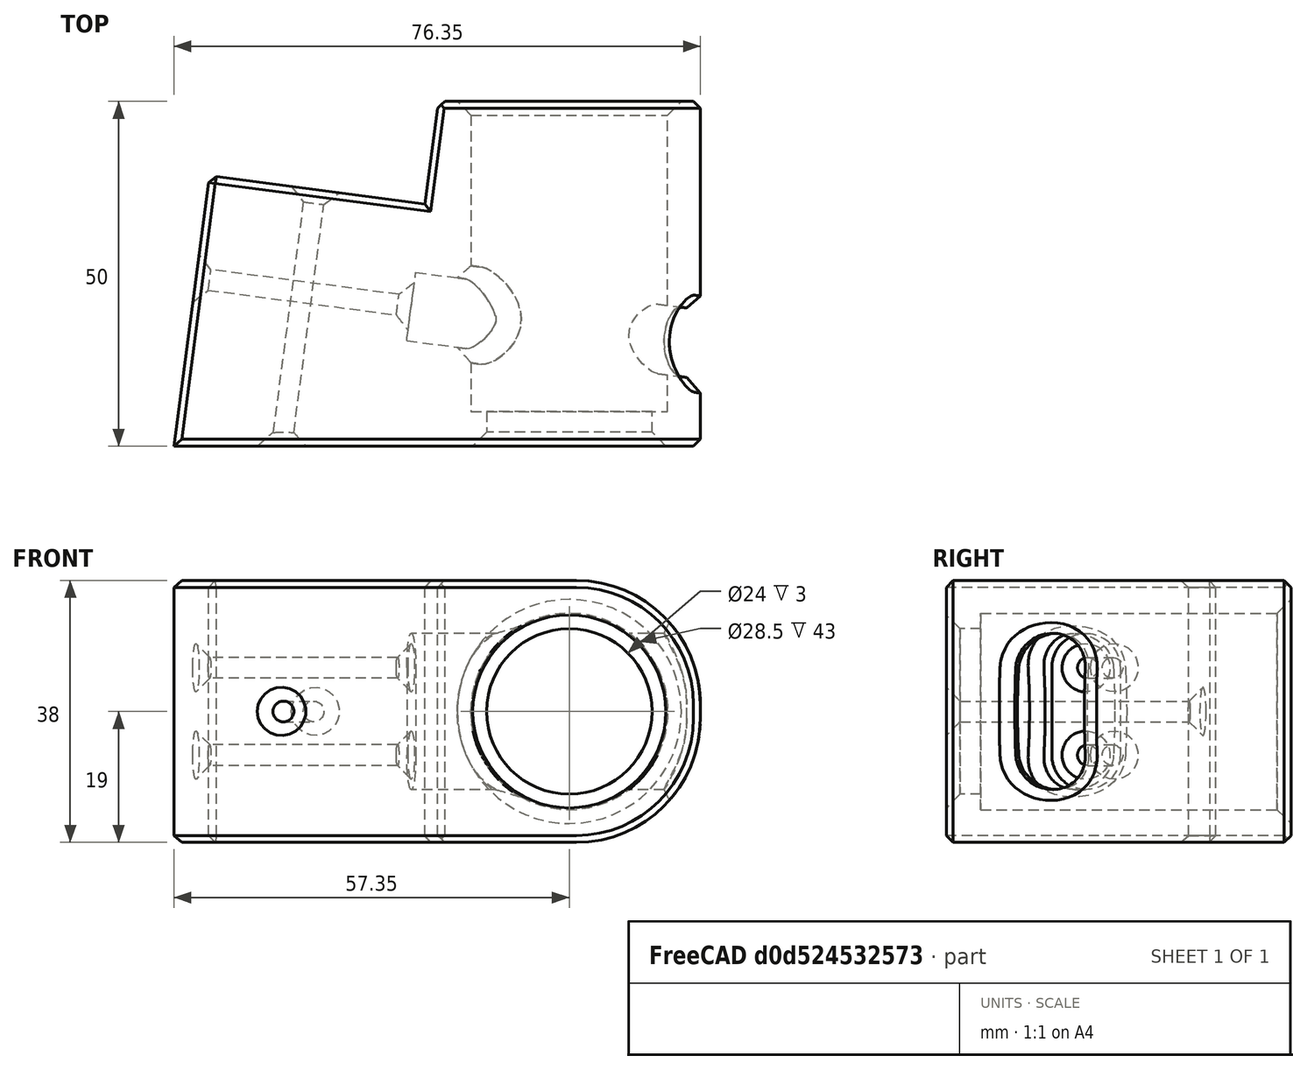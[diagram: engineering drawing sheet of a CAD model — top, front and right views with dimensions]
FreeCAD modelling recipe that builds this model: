
FCSTD DOCUMENT  (FreeCAD 0.18R16110 (Git))
Label: Support_solar_V3
License: All rights reserved
LicenseURL: http://en.wikipedia.org/wiki/All_rights_reserved
objects: PartDesign::Chamfer×13, Sketcher::SketchObject×10, PartDesign::Pocket×6, PartDesign::Pad×4, PartDesign::Fillet×1, PartDesign::Plane×1, PartDesign::Body×1, Mesh::Feature×1
note: 46 computed .brp shape members not serialized (recipe doc carries the construction recipe); baked Part::Feature solids carry a one-line shape summary decoded from their .brp

FEATURE [Sketcher::SketchObject] Sketch
  MapMode = 5
  Support = -> [XY_Plane]
  sketch-geometry (7):
    g0: LineSegment StartX=19 StartY=0 StartZ=0 EndX=-19 EndY=0 EndZ=0
    g1: LineSegment StartX=-61.9779 StartY=-85.1185 StartZ=0 EndX=-19 EndY=-90.7766 EndZ=0
    g2: LineSegment StartX=-19 StartY=-90.7766 StartZ=0 EndX=19 EndY=-90.7766 EndZ=0
    g3: LineSegment StartX=19 StartY=-90.7766 StartZ=0 EndX=19 EndY=0 EndZ=0
    g4: LineSegment StartX=-19 StartY=0 StartZ=0 EndX=-20.9579 EndY=-14.8717 EndZ=0
    g5: LineSegment StartX=-20.9579 StartY=-14.8717 StartZ=0 EndX=-52.1884 EndY=-10.7601 EndZ=0
    g6: LineSegment StartX=-52.1884 StartY=-10.7601 StartZ=0 EndX=-61.9779 EndY=-85.1185 EndZ=0
  constraints (20):
    c: PointOnObject(g0,g-1)
    c: Coincident(g1,g2)
    c: Horizontal(g2)
    c: Coincident(g2,g3)
    c: Coincident(g3,g0)
    c: Vertical(g3)
    c: Coincident(g0,g4)
    c: Coincident(g4,g5)
    c: Coincident(g5,g6)
    c: Coincident(g6,g1)
    c: Angle(g4,g0) = 1.7017
    c: Perpendicular(g4,g5)
    c: Perpendicular(g5,g6)
    c: Perpendicular(g1,g6)
    c: Distance(g5) = 31.5
    c: Distance(g4) = 15
    c: DistanceX(g0,g0) = 38
    c: Distance(g6) = 75
    c: Equal(g2,g0)
    c: Symmetric(g0,g0,g-2)
FEATURE [PartDesign::Pad] Pad
  Length = 38
  Length2 = 100
  Profile = -> Sketch
  Type = 0
FEATURE [Sketcher::SketchObject] Sketch001
  MapMode = 5
  Placement = pos=(0,0,0) rot=(0,0.707107,0.707107;3.14159rad)
  Support = -> [Pad]
  sketch-geometry (1):
    g0: Circle CenterX=0 CenterY=19 CenterZ=0 NormalX=0 NormalY=0 NormalZ=1 AngleXU=0 Radius=14.25
  constraints (3):
    c: Radius(g0) = 14.25
    c: Distance(g-1,g0) = 19
    c: PointOnObject(g0,g-2)
FEATURE [PartDesign::Pocket] Pocket
  BaseFeature = -> Pad
  Length = 100
  Length2 = 100
  Profile = -> Sketch001
  Type = 0
FEATURE [PartDesign::Fillet] Fillet
  Base = -> Pocket [Edge7,Edge8]
  BaseFeature = -> Pocket
  Radius = 18
FEATURE [Sketcher::SketchObject] Sketch002
  ExternalGeometry = -> [Fillet]
  MapMode = 5
  Placement = pos=(-49.9068,6.57036,0) rot=(-0.527011,0.600941,0.600941;4.11164rad)
  Support = -> [Fillet]
  sketch-geometry (4):
    g0: Circle CenterX=32.48 CenterY=25.3333 CenterZ=0 NormalX=0 NormalY=0 NormalZ=1 AngleXU=0 Radius=1.5
    g1: Circle CenterX=32.48 CenterY=12.6667 CenterZ=0 NormalX=0 NormalY=0 NormalZ=1 AngleXU=0 Radius=1.5
    g2: Circle CenterX=77.48 CenterY=25.3333 CenterZ=0 NormalX=0 NormalY=0 NormalZ=1 AngleXU=0 Radius=1.5
    g3: Circle CenterX=77.48 CenterY=12.6667 CenterZ=0 NormalX=0 NormalY=0 NormalZ=1 AngleXU=0 Radius=1.5
  constraints (12):
    c: Radius(g3) = 1.5
    c: Equal(g3,g2)
    c: Equal(g3,g0)
    c: Equal(g3,g1)
    c: Distance(g0,g-3) = 15
    c: Distance(g1,g-3) = 15
    c: Distance(g2,g-5) = 15
    c: Distance(g3,g-5) = 15
    c: DistanceY(g-1,g1) = 12.6667
    c: Distance(g0,g-4) = 12.6667
    c: Distance(g2,g-4) = 12.6667
    c: DistanceY(g-1,g3) = 12.6667
FEATURE [PartDesign::Pocket] Pocket001
  BaseFeature = -> Fillet
  Length = 100
  Length2 = 100
  Profile = -> Sketch002
  Type = 0
FEATURE [PartDesign::Plane] DatumPlane
  Length = 81.0007
  MapMode = 5
  Placement = pos=(-18.6763,2.45878,0) rot=(-0.527011,0.600941,0.600941;4.11164rad)
  ResizeMode = 0
  Support = -> [Pocket001]
  Width = 59.5477
FEATURE [Sketcher::SketchObject] Sketch003
  ExternalGeometry = -> [Pocket001]
  MapMode = 5
  Placement = pos=(-18.6763,2.45878,0) rot=(-0.527011,0.600941,0.600941;4.11164rad)
  Support = -> [DatumPlane]
  sketch-geometry (8):
    g0: ArcOfCircle CenterX=32.48 CenterY=25.3333 CenterZ=0 NormalX=0 NormalY=0 NormalZ=1 AngleXU=0 Radius=5 StartAngle=1.1e-15 EndAngle=3.14159
    g1: ArcOfCircle CenterX=32.48 CenterY=12.6667 CenterZ=0 NormalX=0 NormalY=0 NormalZ=1 AngleXU=0 Radius=5 StartAngle=3.14159 EndAngle=6.28319
    g2: LineSegment StartX=27.48 StartY=25.3333 StartZ=0 EndX=27.48 EndY=12.6667 EndZ=0
    g3: LineSegment StartX=37.48 StartY=25.3333 StartZ=0 EndX=37.48 EndY=12.6667 EndZ=0
    g4: ArcOfCircle CenterX=77.48 CenterY=25.3333 CenterZ=0 NormalX=0 NormalY=0 NormalZ=1 AngleXU=0 Radius=5 StartAngle=0 EndAngle=3.14159
    g5: ArcOfCircle CenterX=77.48 CenterY=12.6667 CenterZ=0 NormalX=0 NormalY=0 NormalZ=1 AngleXU=0 Radius=5 StartAngle=3.14159 EndAngle=6.28319
    g6: LineSegment StartX=72.48 StartY=25.3333 StartZ=0 EndX=72.48 EndY=12.6667 EndZ=0
    g7: LineSegment StartX=82.48 StartY=25.3333 StartZ=0 EndX=82.48 EndY=12.6667 EndZ=0
  constraints (16):
    c: Tangent(g0,g3) = 1.5708
    c: Tangent(g0,g2) = -1.5708
    c: Tangent(g2,g1) = -1.5708
    c: Tangent(g3,g1) = 1.5708
    c: Vertical(g2)
    c: Coincident(g0,g-3)
    c: Coincident(g1,g-4)
    c: Radius(g1) = 5
    c: Tangent(g4,g7) = 1.5708
    c: Tangent(g4,g6) = -1.5708
    c: Tangent(g6,g5) = -1.5708
    c: Tangent(g7,g5) = 1.5708
    c: Vertical(g6)
    c: Coincident(g4,g-5)
    c: Coincident(g5,g-6)
    c: Radius(g5) = 5
FEATURE [PartDesign::Pocket] Pocket002
  BaseFeature = -> Pocket001
  Length = 70
  Length2 = 100
  Profile = -> Sketch003
  Type = 0
FEATURE [Sketcher::SketchObject] Sketch004
  ExternalGeometry = -> [Pocket002,DatumPlane]
  MapMode = 5
  Placement = pos=(-2.2816,-17.3305,0) rot=(0.046297,0.706349,0.706349;3.04907rad)
  Support = -> [Pocket002]
  sketch-geometry (1):
    g0: Circle CenterX=34.8375 CenterY=19 CenterZ=0 NormalX=0 NormalY=0 NormalZ=1 AngleXU=0 Radius=1.5
  constraints (3):
    c: Radius(g0) = 1.5
    c: Distance(g0,g-3) = 19
    c: Distance(g0,g-4) = 15.5
FEATURE [PartDesign::Pocket] Pocket003
  BaseFeature = -> Pocket002
  Length = 50
  Length2 = 100
  Profile = -> Sketch004
  Type = 0
FEATURE [PartDesign::Chamfer] Chamfer
  Base = -> Pocket003 [Edge80,Edge82,Edge83,Edge85,Edge84]
  BaseFeature = -> Pocket003
  Size = 2
FEATURE [PartDesign::Chamfer] Chamfer001
  Base = -> Chamfer [Edge52,Edge48]
  BaseFeature = -> Chamfer
  Size = 2
FEATURE [PartDesign::Chamfer] Chamfer002
  Base = -> Chamfer001 [Edge70]
  BaseFeature = -> Chamfer001
  Size = 2
FEATURE [PartDesign::Chamfer] Chamfer003
  Base = -> Chamfer002 [Edge11]
  BaseFeature = -> Chamfer002
  Size = 2
FEATURE [PartDesign::Chamfer] Chamfer004
  Base = -> Chamfer003 [Edge11]
  BaseFeature = -> Chamfer003
  Size = 2
FEATURE [PartDesign::Chamfer] Chamfer005
  Base = -> Chamfer004 [Edge84]
  BaseFeature = -> Chamfer004
  Size = 1
FEATURE [Sketcher::SketchObject] Sketch006
  MapMode = 5
  Placement = pos=(0,0,38) rot=(0,0,1;0rad)
  sketch-geometry (3):
    g0: LineSegment StartX=1 StartY=-90.7766 StartZ=0 EndX=-61.6371 EndY=-82.5303 EndZ=0
    g1: LineSegment StartX=-61.6371 StartY=-82.5303 StartZ=0 EndX=-62.7228 EndY=-90.7766 EndZ=0
    g2: LineSegment StartX=-62.7228 StartY=-90.7766 StartZ=0 EndX=1 EndY=-90.7766 EndZ=0
  constraints (5):
    c: Coincident(g0,g1)
    c: Coincident(g1,g2)
    c: Coincident(g2,g0)
    c: Horizontal(g2)
    c: Perpendicular(g1,g0)
FEATURE [PartDesign::Pad] Pad002
  BaseFeature = -> Chamfer005
  Length = 38
  Length2 = 100
  Profile = -> Sketch006
  Reversed = true
  Type = 0
FEATURE [Sketcher::SketchObject] Sketch007
  MapMode = 5
  Placement = pos=(0,-90.7766,0) rot=(1,0,0;1.5708rad)
  Support = -> [Pad002]
  sketch-geometry (1):
    g0: Circle CenterX=0 CenterY=19 CenterZ=0 NormalX=0 NormalY=0 NormalZ=1 AngleXU=0 Radius=17
  constraints (3):
    c: PointOnObject(g0,g-2)
    c: Radius(g0) = 17
    c: DistanceY(g-1,g0) = 19
FEATURE [PartDesign::Pad] Pad003
  BaseFeature = -> Pad002
  Length = 5
  Length2 = 100
  Profile = -> Sketch007
  Reversed = true
  Type = 0
FEATURE [Sketcher::SketchObject] Sketch008
  ExternalGeometry = -> [Pad003]
  MapMode = 5
  Placement = pos=(0,-90.7766,0) rot=(1,0,0;1.5708rad)
  Support = -> [Pad003]
  sketch-geometry (1):
    g0: Circle CenterX=0 CenterY=19 CenterZ=0 NormalX=0 NormalY=0 NormalZ=1 AngleXU=0 Radius=12
  constraints (2):
    c: Coincident(g0,g-3)
    c: Radius(g0) = 12
FEATURE [PartDesign::Pocket] Pocket004
  BaseFeature = -> Pad003
  Length = 5
  Length2 = 100
  Profile = -> Sketch008
  Type = 0
FEATURE [PartDesign::Chamfer] Chamfer006
  Base = -> Pocket004 [Edge201]
  BaseFeature = -> Pocket004
  Size = 2
FEATURE [PartDesign::Chamfer] Chamfer007
  Base = -> Chamfer006 [Edge98,Edge194,Edge196,Edge193,Edge207,Edge197,Edge195,Edge175,Edge176]
  BaseFeature = -> Chamfer006
  Size = 1
FEATURE [PartDesign::Chamfer] Chamfer008
  Base = -> Chamfer007 [Edge167]
  BaseFeature = -> Chamfer007
  Size = 1
FEATURE [PartDesign::Chamfer] Chamfer009
  Base = -> Chamfer008 [Edge253,Edge251,Edge257,Edge255]
  BaseFeature = -> Chamfer008
  Size = 2
FEATURE [Sketcher::SketchObject] Sketch009
  MapMode = 5
  Placement = pos=(0,0,0) rot=(1,0,0;3.14159rad)
  Support = -> [Chamfer009]
  sketch-geometry (4):
    g0: LineSegment StartX=-70 StartY=110 StartZ=0 EndX=70 EndY=110 EndZ=0
    g1: LineSegment StartX=70 StartY=110 StartZ=0 EndX=70 EndY=50 EndZ=0
    g2: LineSegment StartX=70 StartY=50 StartZ=0 EndX=-70 EndY=50 EndZ=0
    g3: LineSegment StartX=-70 StartY=50 StartZ=0 EndX=-70 EndY=110 EndZ=0
  constraints (11):
    c: Coincident(g0,g1)
    c: Coincident(g1,g2)
    c: Coincident(g2,g3)
    c: Coincident(g3,g0)
    c: Horizontal(g0)
    c: Vertical(g1)
    c: Vertical(g3)
    c: Symmetric(g1,g2,g-2)
    c: DistanceY(g-1,g2) = 50
    c: DistanceX(g0,g0) = 140
    c: DistanceY(g3,g3) = 60
FEATURE [PartDesign::Pocket] Pocket005
  BaseFeature = -> Chamfer009
  Length = 50
  Length2 = 100
  Profile = -> Sketch009
  Type = 0
FEATURE [Sketcher::SketchObject] Sketch010
  ExternalGeometry = -> [Pocket005]
  MapMode = 5
  Placement = pos=(0,-50,0) rot=(1,0,0;1.5708rad)
  Support = -> [Pocket005]
  sketch-geometry (2):
    g0: Circle CenterX=0 CenterY=19 CenterZ=0 NormalX=0 NormalY=0 NormalZ=1 AngleXU=0 Radius=17
    g1: Circle CenterX=0 CenterY=19 CenterZ=0 NormalX=0 NormalY=0 NormalZ=1 AngleXU=0 Radius=12
  constraints (4):
    c: Coincident(g1,g-3)
    c: Coincident(g0,g1)
    c: Radius(g0) = 17
    c: Radius(g1) = 12
FEATURE [PartDesign::Pad] Pad004
  BaseFeature = -> Pocket005
  Length = 5
  Length2 = 100
  Profile = -> Sketch010
  Reversed = true
  Type = 0
FEATURE [PartDesign::Chamfer] Chamfer010
  Base = -> Pad004 [Edge136]
  BaseFeature = -> Pad004
  Size = 2
FEATURE [PartDesign::Chamfer] Chamfer011
  Base = -> Chamfer010 [Edge16]
  BaseFeature = -> Chamfer010
  Size = 2
FEATURE [PartDesign::Chamfer] Chamfer012
  Base = -> Chamfer011 [Edge2]
  BaseFeature = -> Chamfer011
  Size = 1
FEATURE [PartDesign::Body] Body
  Group = -> [Sketch,Pad,Sketch001,Pocket,Fillet,Sketch002,Pocket001,DatumPlane,Sketch003,Pocket002,Sketch004,Pocket003,Chamfer,Chamfer001,Chamfer002,Chamfer003,Chamfer004,Chamfer005,Sketch006,Pad002,Sketch007,Pad003,Sketch008,Pocket004,Chamfer006,Chamfer007,Chamfer008,Chamfer009,Sketch009,Pocket005,Sketch010,Pad004,Chamfer010,Chamfer011,Chamfer012]
  Origin = -> Origin
  Tip = -> Chamfer012
FEATURE [Mesh::Feature] Mesh  label="Body (Meshed)"
